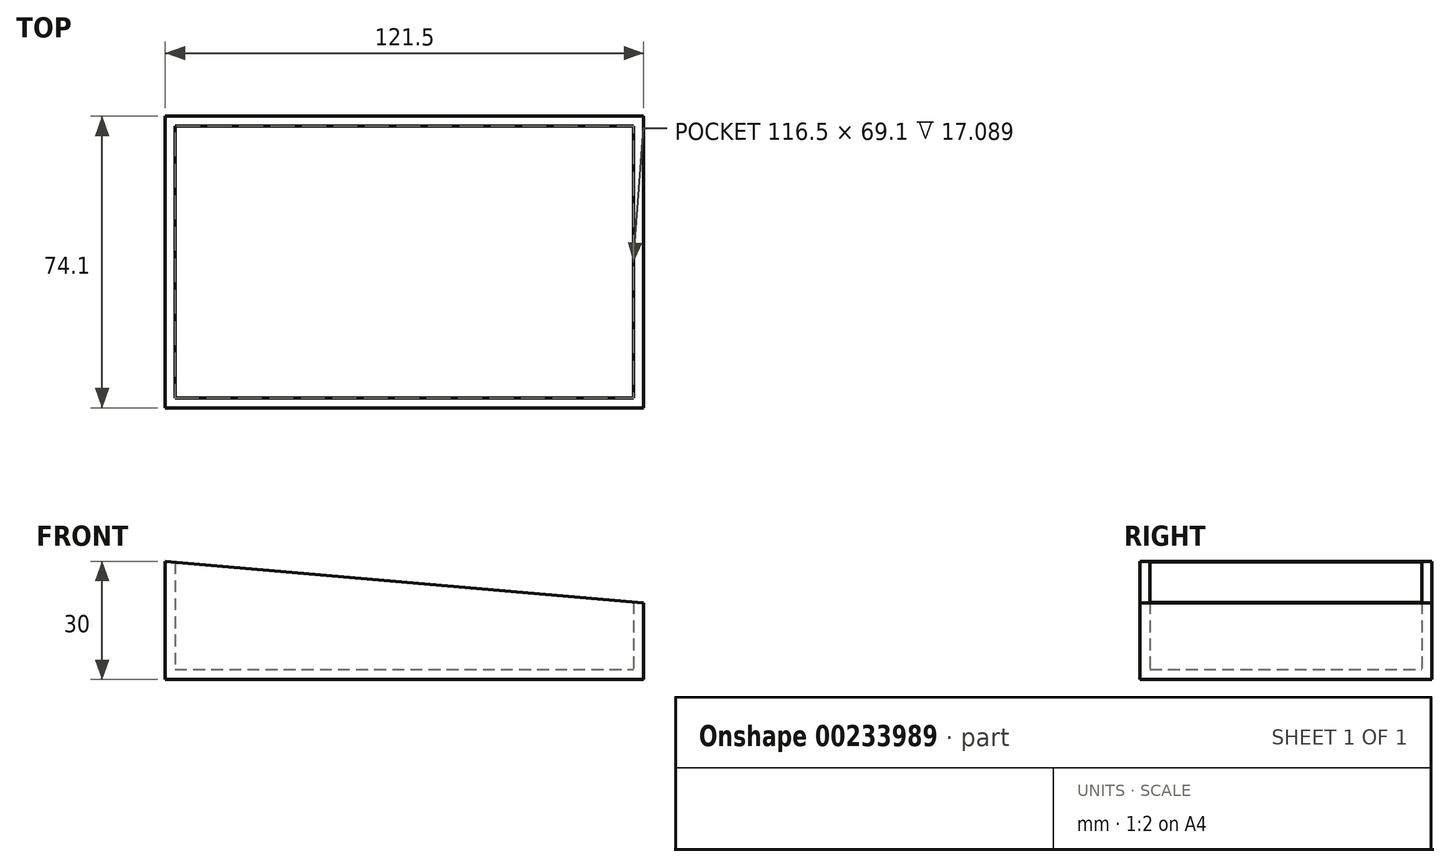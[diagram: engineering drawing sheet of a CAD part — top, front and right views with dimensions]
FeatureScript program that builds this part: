
annotation { "Feature Type Name" : "Feature", "Feature Type Description" : "" }
export const myFeature = defineFeature(function(context is Context, id is Id, definition is map)
    precondition{}
    {
        {
            var Q0;
            Q0=qCreatedBy(makeId("Top.planeOp"),FACE);
            var sketch = newSketch(context, id + "F0", { "sketchPlane" : qUnion([Q0])});
            skLineSegment(sketch, "E0.bottom", {"start": v(-60.75, -37.05) * mm, "end": v(60.75, -37.05) * mm});
            skLineSegment(sketch, "E0.top", {"start": v(-60.75, 37.05) * mm, "end": v(60.75, 37.05) * mm});
            skLineSegment(sketch, "E0.left", {"start": v(-60.75, -37.05) * mm, "end": v(-60.75, 37.05) * mm});
            skLineSegment(sketch, "E0.right", {"start": v(60.75, -37.05) * mm, "end": v(60.75, 37.05) * mm});
            skPoint(sketch, "E0.middle", {"position": v(0, 0) * mm});
            skSolve(sketch);
        }
        {
            var Q0;
            Q0 = qSketchRegion(id + "F0", true);
            extrude(context, id + "F1", {"entities" : qUnion([Q0]), "depth" : 30 * mm});
        }
        {
            var Q0;
            Q0=makeQuery(id+"F1.opExtrude","CAP_FACE",FACE,{"disambiguationData":[OSD([sQuery(id+"F0.wireOp",EDGE,"E0.bottom"),sQuery(id+"F0.wireOp",EDGE,"E0.top"),sQuery(id+"F0.wireOp",EDGE,"E0.left"),sQuery(id+"F0.wireOp",EDGE,"E0.right")])],"isStart":false});
            var Q1;
            Q1=makeQuery(id+"F1.opExtrude","SWEPT_BODY",BODY,{"disambiguationData":[OSD([sQuery(id+"F0.wireOp",EDGE,"E0.bottom"),sQuery(id+"F0.wireOp",EDGE,"E0.top"),sQuery(id+"F0.wireOp",EDGE,"E0.left"),sQuery(id+"F0.wireOp",EDGE,"E0.right")])]});
            shell(context, id + "F2", {"entities" : qUnion([Q0]), "parts" : qUnion([Q1]), "thickness" : 2.5 * mm});
        }
        {
            var Q0;
            Q0=makeQuery(id+"F1.opExtrude","SWEPT_FACE",FACE,{"disambiguationData":[OSD([sQuery(id+"F0.wireOp",EDGE,"E0.top")])]});
            var sketch = newSketch(context, id + "F3", { "sketchPlane" : qUnion([Q0])});
            skLineSegment(sketch, "E1", {"start": v(60.75, 30) * mm, "end": v(-60.75, 19.37) * mm});
            skSolve(sketch);
        }
        {
            var Q0;
            Q0=makeQuery(id+"F1.opExtrude","SWEPT_FACE",FACE,{"disambiguationData":[OSD([sQuery(id+"F0.wireOp",EDGE,"E0.bottom")])]});
            var sketch = newSketch(context, id + "F4", { "sketchPlane" : qUnion([Q0])});
            skLineSegment(sketch, "E2", {"start": v(-60.75, 30) * mm, "end": v(60.75, 19.37) * mm});
            skSolve(sketch);
        }
        {
            var Q0;
            {var subQ0=sQuery(id+"F3.wireOp",EDGE,"E1");Q0=makeQuery(id+"F3.imprint","IMPRINT",FACE,{"disambiguationData":[TD([[makeQuery(id+"F3.imprint","IMPRINT",EDGE,{"derivedFrom":subQ0}),-1.0]])]});}
            extrude(context, id + "F5", {"entities" : qUnion([Q0]), "operationType" : NewBodyOperationType.REMOVE, "oppositeDirection" : true, "depth" : 79.2 * mm});
        }
    });
